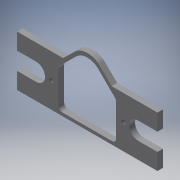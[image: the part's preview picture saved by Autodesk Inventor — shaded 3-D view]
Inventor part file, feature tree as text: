
AUTODESK INVENTOR PART (.ipt)
format: ipt  version: 2016 (Build 200138000, 138)  size: 202,240 bytes
history: native  units: mm (DEFAULTED — no unit token found)
features: other x11, extrude x5, hole x2, sketch x2
ambient origin geometry x8: Origin, YZ Plane, XZ Plane, XY Plane, X Axis, Y Axis, Z Axis, Center Point
bodies: Solid1 (feature_tree)
feature tree (20):
  other  "Blocks"
  extrude  "Extrusion1"  Depth=1.016mm TaperAngle=0.0deg
  extrude  "Extrusion2"  Depth=0.762mm
  extrude  "Extrusion3"  Depth=0.762mm
  extrude  "Extrusion8"  Depth=1.016mm TaperAngle=0.0deg
  extrude  "Extrusion7"  Depth=1.016mm TaperAngle=0.0deg
  hole  "Hole9"  [1 undecoded]
  hole  "Hole10"  [1 undecoded]
  other  "Block1"
  other  "Block2"
  other  "Block3"
  other  "Block4"
  sketch  "Sketch12"  dims[d2=1.016mm d3=0.0mm d10=1.016mm d11=0.0mm]
  sketch  "Sketch13"  dims[d20=1.016mm d21=0.0mm d110=0.762mm d111=0.762mm d117=1.016mm d118=0.0mm d132=1.016mm d133=0.0mm d149=0.762mm d150=0.762mm d153=0.762mm d154=0.762mm d173=25.4mm d174=25.4mm d157=0.7366mm d158=1.524mm d159=9.525mm d160=6.35mm d161=14.3117mm d162=1.524mm d163=0.0mm d177=25.4mm d178=25.4mm d166=0.7366mm d167=1.7272mm d168=9.525mm d169=6.35mm d170=14.3117mm d171=2.794mm d172=0.0mm d22=25.4mm d23=25.4mm d63=25.4mm d64=25.4mm d81=25.4mm d82=25.4mm d108=25.4mm d109=25.4mm d155=25.4mm d156=25.4mm]
  other  "Block5"
  other  "Block6"
  other  "Block1:2"
  other  "Block2:2"
  other  "Block3:2"
  other  "Block6:1"
note: 2 required parameter values undecoded (feature->parameter linkage not recoverable at this tier; creation-order binding heuristic only, values carry confidence <= 0.55)
